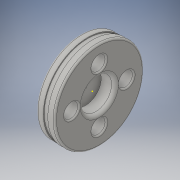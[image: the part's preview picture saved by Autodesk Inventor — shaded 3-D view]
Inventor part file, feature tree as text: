
AUTODESK INVENTOR PART (.ipt)
format: ipt  version: 2016 (Build 200138000, 138)  size: 272,896 bytes
history: native  units: in
note: dims shown in document units (in); Inventor stores cm internally (conversion verified against a paired STEP export)
features: sketch x10, extrude x7, fillet x3
ambient origin geometry x8: Origin, YZ Plane, XZ Plane, XY Plane, X Axis, Y Axis, Z Axis, Center Point
bodies: Solid1 (feature_tree)
feature tree (20):
  extrude  "Extrusion1"  Depth=0.139in TaperAngle=0.0deg
  sketch  "Sketch2"  dims[d3=0.2in d4=0.0in d5=0.2in d6=0.0in]
  extrude  "Extrusion2"  Depth=0.2in TaperAngle=0.0deg
  extrude  "Extrusion3"  Depth=1.5748in TaperAngle=360.0deg
  extrude  "Extrusion5"  Depth=0.05in
  sketch  "Sketch6"  dims[d23=1.0in d24=0.0in]
  extrude  "Extrusion6"  Depth=0.1in
  fillet  "Fillet2"  Radius=0.04in
  extrude  "Extrusion7"  [1 undecoded]
  fillet  "Fillet3"  [1 undecoded]
  fillet  "Fillet4"  [1 undecoded]
  extrude  "Extrusion8"  [1 undecoded]
  sketch  "Sketch10"
  sketch  "Sketch1"  dims[d0=2.5in d1=0.139in d2=0.0in]
  sketch  "Sketch3"  dims[d10=0.079in d11=0.0in d12=1.5748in d14=360.0deg]
  sketch  "Sketch4"  dims[d16=5.0in d17=0.0in d18=0.05in]
  sketch  "Sketch5"  dims[d19=0.4in d20=0.0in d21=0.1in d22=0.04in]
  sketch  "Sketch7"
  sketch  "Sketch8"
  sketch  "Sketch9"
note: 4 required parameter values undecoded (feature->parameter linkage not recoverable at this tier; creation-order binding heuristic only, values carry confidence <= 0.55)
